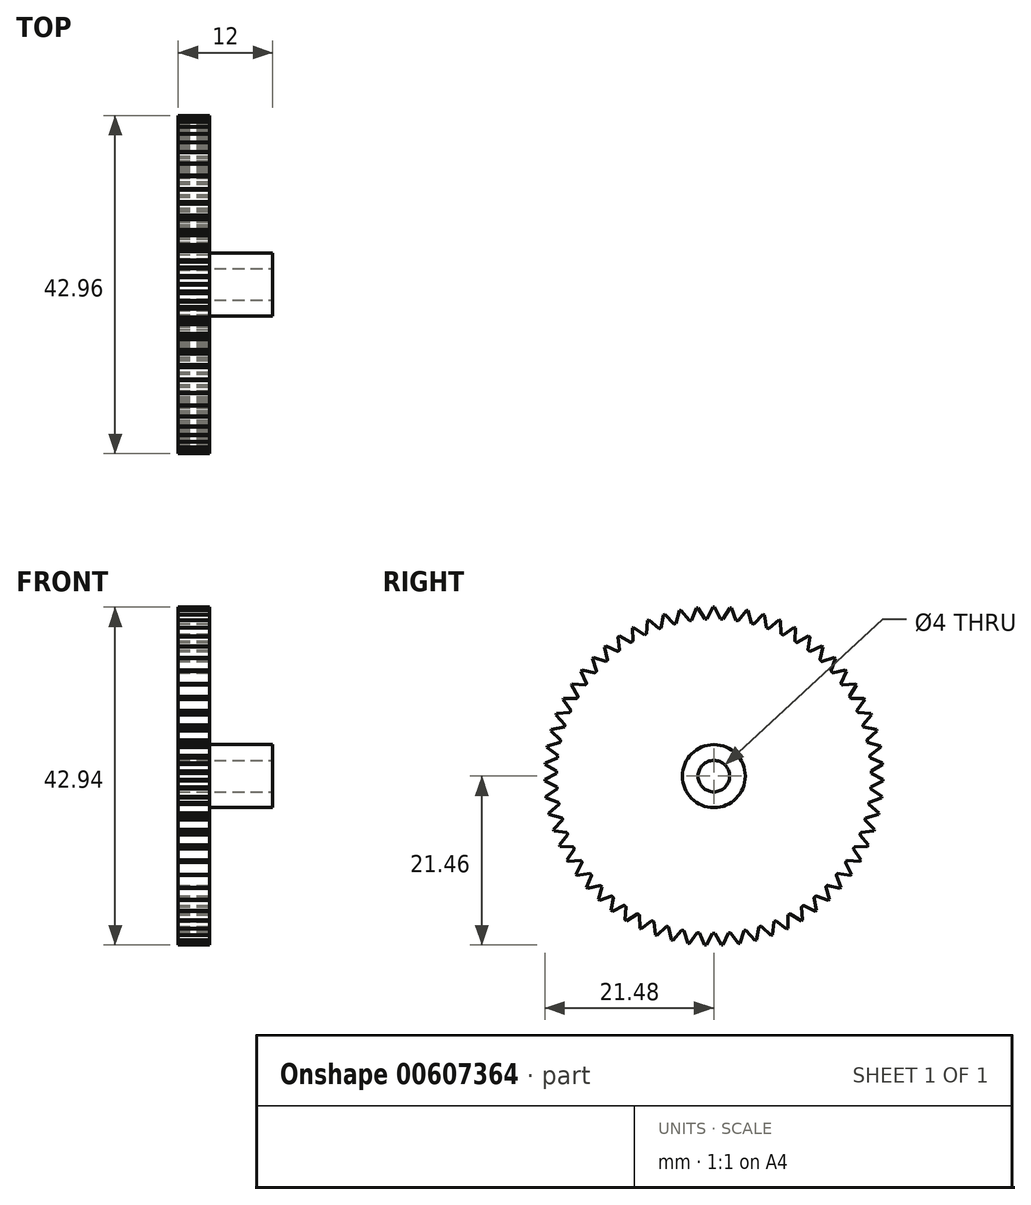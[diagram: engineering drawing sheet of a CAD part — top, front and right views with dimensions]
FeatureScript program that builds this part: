
annotation { "Feature Type Name" : "Feature", "Feature Type Description" : "" }
export const myFeature = defineFeature(function(context is Context, id is Id, definition is map)
    precondition{}
    {
        {
            var Q0;
            Q0=qCreatedBy(makeId("Top.planeOp"),FACE);
            var sketch = newSketch(context, id + "F0", { "sketchPlane" : qUnion([Q0])});
            skLineSegment(sketch, "E0", {"start": v(-2, 0) * mm, "end": v(2, 0) * mm});
            skLineSegment(sketch, "E1", {"start": v(-2, 0) * mm, "end": v(-2, 20) * mm});
            skLineSegment(sketch, "E2.MirrorCS", {"start": v(2, 0) * mm, "end": v(2, 20) * mm});
            skLineSegment(sketch, "E3", {"start": v(-2, 20) * mm, "end": v(2, 20) * mm});
            skSolve(sketch);
        }
        {
            var Q0;
            Q0=qCreatedBy(makeId("Right.planeOp"),FACE);
            var sketch = newSketch(context, id + "F1", { "sketchPlane" : qUnion([Q0])});
            skCircle(sketch, "E4", {"center": v(0, 0) * mm, "radius": 5 * mm});
            skSolve(sketch);
        }
        {
            var Q0;
            Q0=makeQuery(id+"F0.imprint","IMPRINT",FACE,{"disambiguationData":[TD([[makeQuery(id+"F0.imprint","IMPRINT",EDGE,{"derivedFrom":sQuery(id+"F0.wireOp",EDGE,"E0")}),1.0]])]});
            var Q1;
            Q1=sQuery(id+"F1.wireOp",EDGE,"E4");
            sweep(context, id + "F2", {"profiles" : qUnion([Q0]), "path" : qUnion([Q1])});
        }
        {
            var Q0;
            Q0=makeQuery(id+"F2.opSweep","SWEPT_FACE",FACE,{"disambiguationData":[OSD([sQuery(id+"F0.wireOp",EDGE,"E2.MirrorCS"),sQuery(id+"F1.wireOp",EDGE,"E4")])]});
            var sketch = newSketch(context, id + "F3", { "sketchPlane" : qUnion([Q0])});
            skLineSegment(sketch, "E5", {"start": v(0, 19.5) * mm, "end": v(0, 20) * mm, "construction": true});
            skLineSegment(sketch, "E6", {"start": v(0.1, 21.48) * mm, "end": v(-0.1, 21.48) * mm});
            skLineSegment(sketch, "E7", {"start": v(0.85, 19.98) * mm, "end": v(0.1, 21.48) * mm});
            skLineSegment(sketch, "E8.MirrorCS", {"start": v(-0.85, 19.98) * mm, "end": v(-0.1, 21.48) * mm});
            skLineSegment(sketch, "E9", {"start": v(-0.85, 19.98) * mm, "end": v(0.85, 19.98) * mm});
            skLineSegment(sketch, "E10", {"start": v(0, 21.48) * mm, "end": v(0, 19.98) * mm, "construction": true});
            skCircle(sketch, "E11", {"center": v(0, 0) * mm, "radius": 2 * mm});
            skCircle(sketch, "E12", {"center": v(0, 0) * mm, "radius": 4 * mm});
            skSolve(sketch);
        }
        {
            var Q0;
            Q0=makeQuery(id+"F3.imprint","IMPRINT",FACE,{"disambiguationData":[TD([[makeQuery(id+"F3.imprint","IMPRINT",EDGE,{"derivedFrom":sQuery(id+"F3.wireOp",EDGE,"E6")}),1.0]])]});
            extrude(context, id + "F4", {"entities" : qUnion([Q0]), "operationType" : NewBodyOperationType.ADD, "oppositeDirection" : true, "depth" : 4 * mm, "offsetDistance" : 25 * mm});
        }
        {
            var Q0;
            Q0=makeQuery(id+"F4.opExtrude","SWEPT_FACE",FACE,{"disambiguationData":[OSD([sQuery(id+"F3.wireOp",EDGE,"E7")])]});
            var Q1;
            Q1=makeQuery(id+"F4.opExtrude","SWEPT_FACE",FACE,{"disambiguationData":[OSD([sQuery(id+"F3.wireOp",EDGE,"E6")])]});
            var Q2;
            Q2=makeQuery(id+"F4.opExtrude","SWEPT_FACE",FACE,{"disambiguationData":[OSD([sQuery(id+"F3.wireOp",EDGE,"E8.MirrorCS")])]});
            var Q3;
            Q3=makeQuery(id+"F2.opSweep","SWEPT_FACE",FACE,{"disambiguationData":[OSD([sQuery(id+"F0.wireOp",EDGE,"E3"),sQuery(id+"F1.wireOp",EDGE,"E4")])]});
            circularPattern(context, id + "F5", {"patternType" : PatternType.FACE, "faces" : qUnion([Q0, Q1, Q2]), "axis" : qUnion([Q3]), "angle" : 360 * degree, "instanceCount" : 63, "oppositeDirection" : true, "equalSpace" : true});
        }
        {
            var Q0;
            Q0=makeQuery(id+"F3.imprint","IMPRINT",FACE,{"disambiguationData":[TD([[makeQuery(id+"F3.imprint","IMPRINT",EDGE,{"derivedFrom":sQuery(id+"F3.wireOp",EDGE,"E11")}),1.0]])]});
            extrude(context, id + "F6", {"entities" : qUnion([Q0]), "operationType" : NewBodyOperationType.REMOVE, "oppositeDirection" : true, "depth" : 4 * mm, "offsetDistance" : 25 * mm});
        }
        {
            var Q0;
            Q0=makeQuery(id+"F3.imprint","IMPRINT",FACE,{"disambiguationData":[TD([[makeQuery(id+"F3.imprint","IMPRINT",EDGE,{"derivedFrom":sQuery(id+"F3.wireOp",EDGE,"E11")}),-1.0]])]});
            extrude(context, id + "F7", {"entities" : qUnion([Q0]), "operationType" : NewBodyOperationType.ADD, "depth" : 8 * mm, "offsetDistance" : 25 * mm});
        }
    });
